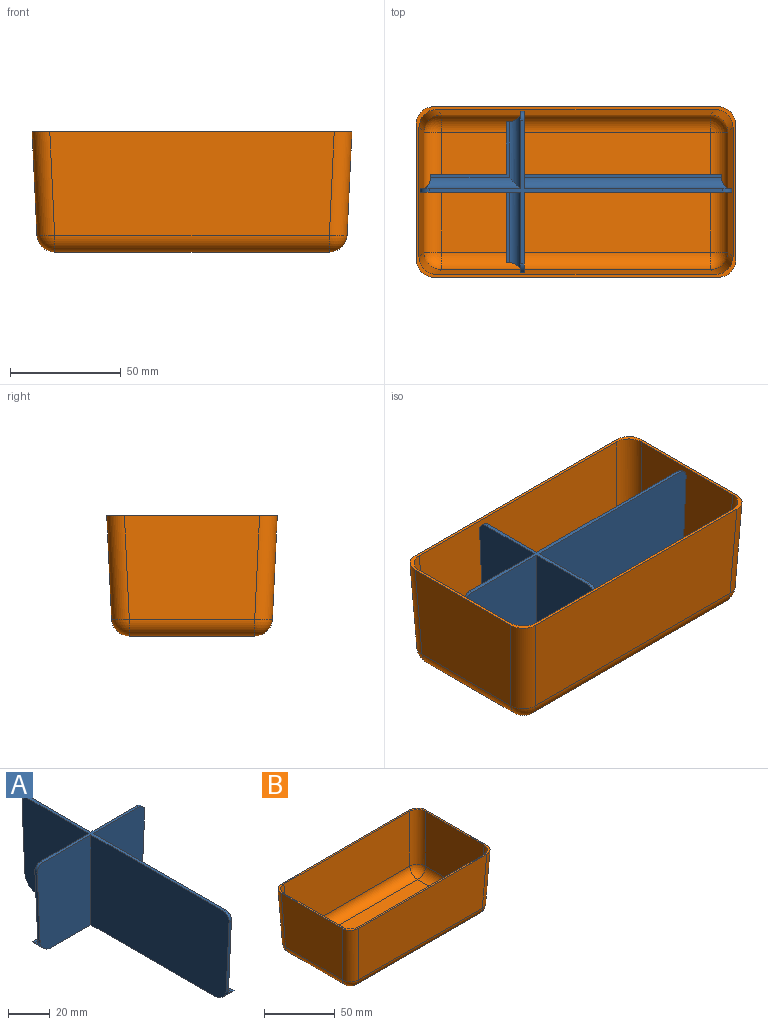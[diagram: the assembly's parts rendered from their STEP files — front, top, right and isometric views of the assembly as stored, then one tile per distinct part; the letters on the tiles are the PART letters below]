
ASSEMBLY  parts=2 mates=1
PART A: 33 faces, bbox 73.1x140.8x53 mm
  f0: plane 34.26x2mm, normal (1,0,0), area 65.2mm2, adj f7,f8,f17,f23
  f1: plane 89.26x2mm, normal (1,0,0), area 175.2mm2, adj f2,f7,f19,f24
  f2: plane 89.26x1.4mm, normal (0,0,1), area 125mm2, adj f1,f19,f24,f25
  f3: plane 46x45.31mm, normal (1,0,0), area 2039.3mm2, adj f9,f11,f18,f23,f26,f31
  f4: plane 93.91x46mm, normal (1,0,0), area 4274.9mm2, adj f9,f10,f19,f24,f25,f32
  f5: plane 53x45.31mm, normal (-1,0,0), area 2311mm2, adj f7,f9,f11,f13,f14,f15,f23,f28
  f6: plane 93.91x53mm, normal (-1,0,0), area 4904.9mm2, adj f7,f9,f10,f16,f24,f32
  f7: plane 120.94x53.24mm, normal (0,0,-1), area 1329.4mm2, adj f0,f1,f5,f6,f15,f16,f17,f19
  f8: plane 35.66x25.31mm, normal (0,0,1), area 83.4mm2, adj f0,f17,f22,f23,f26,f27
  f9: plane 132.81x65.11mm, normal (0,0,1), area 314.1mm2, adj f3,f4,f5,f6,f13,f16,f18,f19
  f10: plane 41.19x1.94mm, normal (0,-1,-0.05), area 66mm2, adj f4,f6,f24,f32
  f11: plane 41.19x1.94mm, normal (0,1,-0.05), area 66mm2, adj f3,f5,f23,f31
  f12: plane 41.19x1.94mm, normal (-1,0,-0.05), area 66mm2, adj f13,f16,f21,f29
  f13: plane 46x36.56mm, normal (0,1,0), area 1636.8mm2, adj f5,f9,f12,f21,f28,f29
  f14: plane 31.91x1.4mm, normal (0,0,1), area 44.7mm2, adj f5,f15,f21,f28
  f15: plane 31.91x2mm, normal (0,1,0), area 60.5mm2, adj f5,f7,f14,f21
  f16: plane 53x36.56mm, normal (0,-1,0), area 1865.4mm2, adj f6,f7,f9,f12,f21,f29
  f17: plane 23.91x2mm, normal (0,1,0), area 44.5mm2, adj f0,f7,f8,f22
  f18: plane 46x34.96mm, normal (0,1,0), area 1563.2mm2, adj f3,f9,f20,f22,f27,f30
  f19: plane 53x34.96mm, normal (0,-1,0), area 1762.4mm2, adj f1,f2,f4,f7,f9,f20,f22,f25
  f20: plane 41.19x1.94mm, normal (1,0,-0.05), area 66mm2, adj f18,f19,f22,f30
  f21: cylinder r=8mm len=8mm, axis (0,1,0), area 63.5mm2, adj f7,f12,f13,f14,f15,f16,f28
  f22: cylinder r=8mm len=8mm, axis (0,1,0), area 63.5mm2, adj f7,f8,f17,f18,f19,f20,f27
  f23: cylinder r=8mm len=8mm, axis (1,0,0), area 63.5mm2, adj f0,f3,f5,f7,f8,f11,f26
  f24: cylinder r=8mm len=8mm, axis (1,0,0), area 63.5mm2, adj f1,f2,f4,f6,f7,f10,f25
  f25: cylinder r=5mm len=91.91mm, axis (0,1,0), area 711.2mm2, adj f2,f4,f19,f24
  f26: cylinder r=5mm len=43.31mm, axis (0,1,0), area 315.2mm2, adj f3,f8,f23,f27
  f27: cylinder r=5mm len=32.96mm, axis (-1,0,0), area 233.9mm2, adj f8,f18,f22,f26
  f28: cylinder r=5mm len=34.56mm, axis (-1,0,0), area 260.8mm2, adj f5,f13,f14,f21
  f29: cylinder r=4mm len=4.19mm, axis (0,-1,0), area 10.4mm2, adj f9,f12,f13,f16
  f30: cylinder r=4mm len=4.19mm, axis (0,-1,0), area 10.4mm2, adj f9,f18,f19,f20
  f31: cylinder r=4mm len=4.19mm, axis (-1,0,0), area 10.4mm2, adj f3,f5,f9,f11
  f32: cylinder r=4mm len=4.19mm, axis (-1,0,0), area 10.4mm2, adj f4,f6,f9,f10
PART B: 35 faces, bbox 144.6x77.1x54.5 mm
  f0: plane 61.12x46.68mm, normal (1,0,-0.05), area 2753.1mm2, adj f8,f13,f16,f26
  f1: plane 128.62x46.68mm, normal (0,1,-0.05), area 5907.3mm2, adj f8,f13,f14,f22
  f2: plane 61.12x46.68mm, normal (-1,0,-0.05), area 2753.1mm2, adj f8,f14,f15,f19
  f3: plane 58.52x45.38mm, normal (1,0,0.05), area 2561.1mm2, adj f8,f9,f12,f32
  f4: plane 126.02x45.38mm, normal (0,-1,0.05), area 5627.4mm2, adj f8,f9,f10,f28
  f5: plane 58.52x45.38mm, normal (-1,0,0.05), area 2561.1mm2, adj f8,f10,f11,f29
  f6: plane 126.02x45.38mm, normal (0,1,0.05), area 5627.4mm2, adj f8,f11,f12,f33
  f7: plane 128.62x46.68mm, normal (0,-1,-0.05), area 5907.3mm2, adj f8,f15,f16,f23
  f8: plane 144.6x77.1mm, normal (0,0,1), area 569.7mm2, adj f0,f1,f2,f3,f4,f5,f6,f7
  f9: cylinder r=8mm len=45.69mm, axis (0.05,-0.05,-1), area 572mm2, adj f3,f4,f8,f30
  f10: cylinder r=8mm len=45.69mm, axis (-0.05,-0.05,-1), area 572mm2, adj f4,f5,f8,f27
  f11: cylinder r=8mm len=45.69mm, axis (-0.05,0.05,-1), area 572mm2, adj f5,f6,f8,f31
  f12: cylinder r=8mm len=45.69mm, axis (0.05,0.05,-1), area 572mm2, adj f3,f6,f8,f34
  f13: cylinder r=8mm len=46.99mm, axis (0.05,0.05,1), area 588.3mm2, adj f0,f1,f8,f24
  f14: cylinder r=8mm len=46.99mm, axis (-0.05,0.05,1), area 588.3mm2, adj f1,f2,f8,f20
  f15: cylinder r=8mm len=46.99mm, axis (-0.05,-0.05,1), area 588.3mm2, adj f2,f7,f8,f21
  f16: cylinder r=8mm len=46.99mm, axis (0.05,-0.05,1), area 588.3mm2, adj f0,f7,f8,f25
  f17: plane 121.74x54.24mm, normal (0,0,1), area 6602.8mm2, adj f28,f29,f32,f33
  f18: plane 124.22x56.72mm, normal (0,0,-1), area 7044.9mm2, adj f19,f22,f23,f26
  f19: cylinder r=8mm len=56.72mm, axis (0,1,0), area 691.3mm2, adj f2,f18,f20,f21
  f20: sphere r=8mm, area 94.5mm2, adj f14,f19,f22
  f21: sphere r=8mm, area 94.5mm2, adj f15,f19,f23
  f22: cylinder r=8mm len=124.22mm, axis (1,0,0), area 1514.1mm2, adj f1,f18,f20,f24
  f23: cylinder r=8mm len=124.22mm, axis (1,0,0), area 1514.1mm2, adj f7,f18,f21,f25
  f24: sphere r=8mm, area 94.5mm2, adj f13,f22,f26
  f25: sphere r=8mm, area 94.5mm2, adj f16,f23,f26
  f26: cylinder r=8mm len=56.72mm, axis (0,-1,0), area 691.3mm2, adj f0,f18,f24,f25
  f27: sphere r=8mm, area 94.5mm2, adj f10,f28,f29
  f28: cylinder r=8mm len=121.74mm, axis (-1,0,0), area 1483.9mm2, adj f4,f17,f27,f30
  f29: cylinder r=8mm len=54.24mm, axis (0,-1,0), area 661.1mm2, adj f5,f17,f27,f31
  f30: sphere r=8mm, area 94.5mm2, adj f9,f28,f32
  f31: sphere r=8mm, area 94.5mm2, adj f11,f29,f33
  f32: cylinder r=8mm len=54.24mm, axis (0,-1,0), area 661.1mm2, adj f3,f17,f30,f34
  f33: cylinder r=8mm len=121.74mm, axis (-1,0,0), area 1483.9mm2, adj f6,f17,f31,f34
  f34: sphere r=8mm, area 94.5mm2, adj f12,f32,f33
PLACE A rot(axis=(0,0,1),90deg) t=(1.07,17.8,-0.08)mm
PLACE B t=(1.07,17.8,-0.08)mm
MATE revolute A.f7 <-> B.f17  axis (0,0,1) through (1.07,17.8,-0.08)mm
